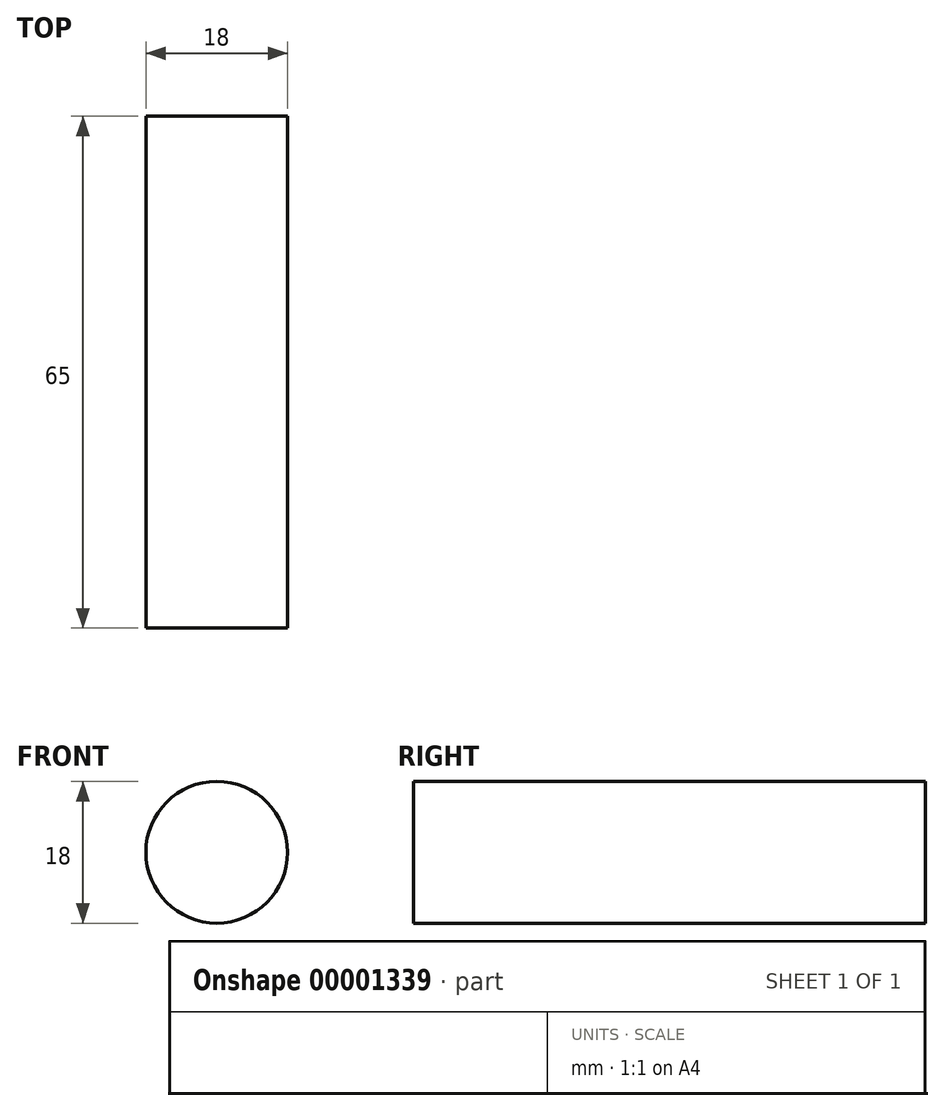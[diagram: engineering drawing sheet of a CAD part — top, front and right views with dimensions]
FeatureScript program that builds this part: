
annotation { "Feature Type Name" : "Feature", "Feature Type Description" : "" }
export const myFeature = defineFeature(function(context is Context, id is Id, definition is map)
    precondition{}
    {
        {
            var Q0;
            Q0=qCreatedBy(makeId("Front.planeOp"),FACE);
            var sketch = newSketch(context, id + "F0", { "sketchPlane" : qUnion([Q0])});
            skCircle(sketch, "E0", {"center": v(0, 0) * mm, "radius": 9 * mm});
            skSolve(sketch);
        }
        {
            var Q0;
            Q0=makeQuery(id+"F0.imprint","IMPRINT",FACE,{"disambiguationData":[TD([[makeQuery(id+"F0.imprint","IMPRINT",EDGE,{"derivedFrom":sQuery(id+"F0.wireOp",EDGE,"E0")}),1.0]])]});
            extrude(context, id + "F1", {"entities" : qUnion([Q0]), "depth" : 65 * mm});
        }
    });
